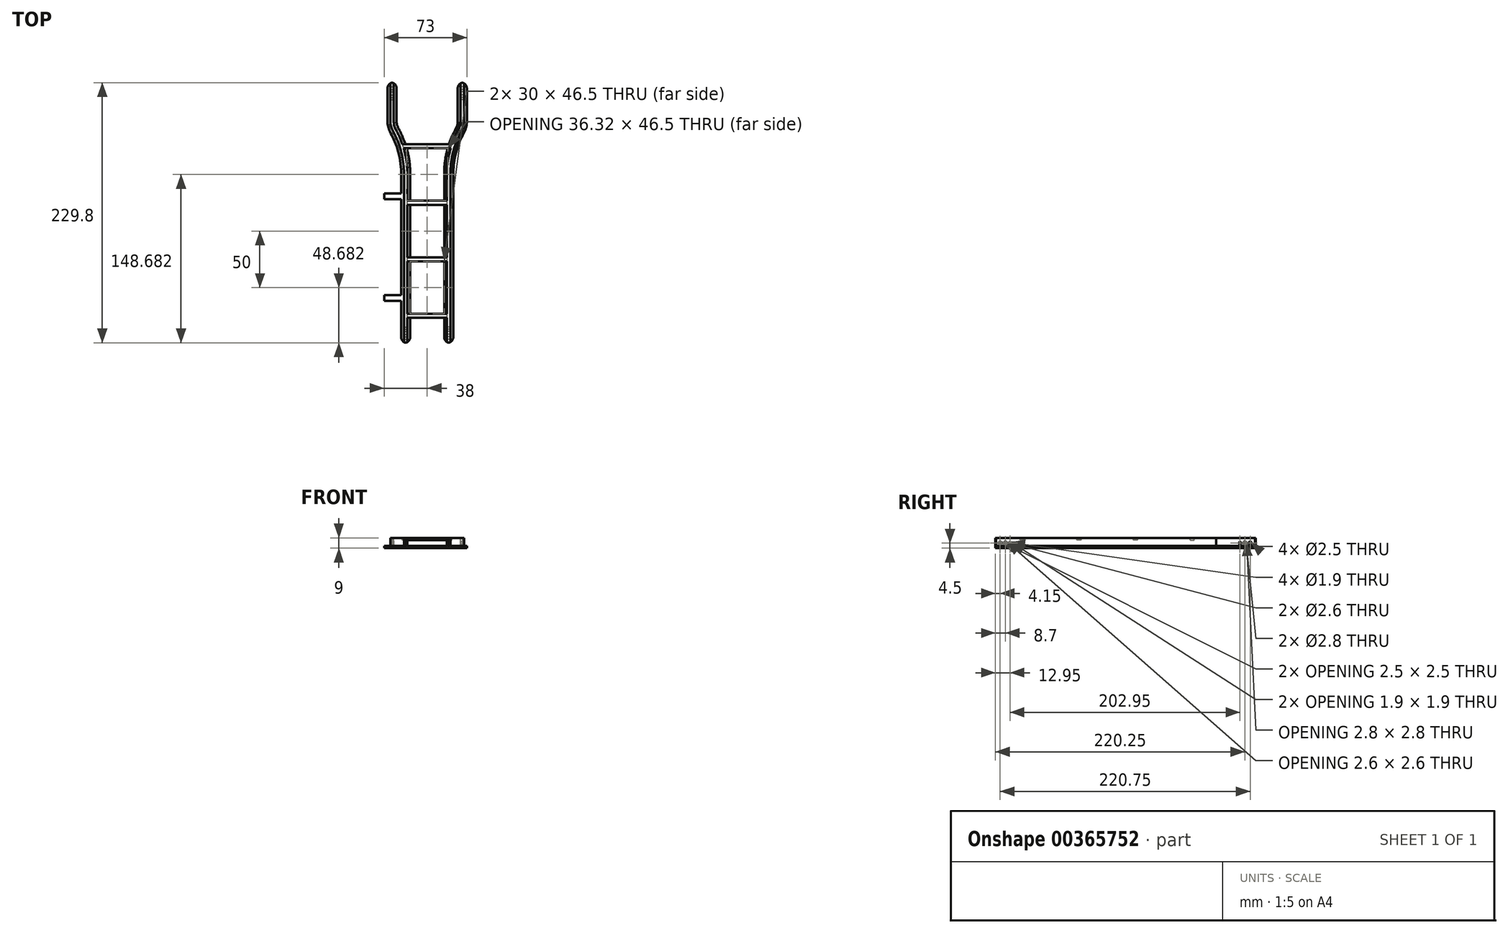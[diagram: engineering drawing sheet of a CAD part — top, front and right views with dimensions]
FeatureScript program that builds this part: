
annotation { "Feature Type Name" : "Feature", "Feature Type Description" : "" }
export const myFeature = defineFeature(function(context is Context, id is Id, definition is map)
    precondition{}
    {
        {
            var Q0;
            Q0=qCreatedBy(makeId("Front.planeOp"),FACE);
            var sketch = newSketch(context, id + "F0", { "sketchPlane" : qUnion([Q0])});
            skLineSegment(sketch, "E0.bottom", {"start": v(-15, 0) * mm, "end": v(-23, 0) * mm});
            skLineSegment(sketch, "E0.top", {"start": v(-15, 9) * mm, "end": v(-23, 9) * mm});
            skLineSegment(sketch, "E0.left", {"start": v(-15, 0) * mm, "end": v(-15, 2) * mm});
            skLineSegment(sketch, "E0.right", {"start": v(-23, 0) * mm, "end": v(-23, 2) * mm});
            skLineSegment(sketch, "E1.bottom", {"start": v(-23, 7) * mm, "end": v(-21, 7) * mm});
            skLineSegment(sketch, "E1.top", {"start": v(-23, 2) * mm, "end": v(-21, 2) * mm});
            skLineSegment(sketch, "E1.right", {"start": v(-20.5, 6.5) * mm, "end": v(-20.5, 2.5) * mm});
            skLineSegment(sketch, "E2.bottom", {"start": v(-17, 7) * mm, "end": v(-15, 7) * mm});
            skLineSegment(sketch, "E2.top", {"start": v(-17, 2) * mm, "end": v(-15, 2) * mm});
            skLineSegment(sketch, "E2.left", {"start": v(-17.5, 6.5) * mm, "end": v(-17.5, 2.5) * mm});
            skLineSegment(sketch, "E3", {"start": v(-19, 9) * mm, "end": v(-19, -4.59) * mm, "construction": true});
            skPoint(sketch, "E3.endSnap0", {"position": v(-19, 0) * mm});
            skLineSegment(sketch, "E4.trimOffspring", {"start": v(-15, 7) * mm, "end": v(-15, 9) * mm});
            skLineSegment(sketch, "E5.trimOffspring", {"start": v(-23, 7) * mm, "end": v(-23, 9) * mm});
            skPoint(sketch, "E6.visualSharp", {"position": v(-20.5, 7) * mm});
            skArc(sketch, "E6.filletArc", {"start": v(-20.5, 6.5) * mm, "mid": v(-20.65, 6.85) * mm, "end": v(-21, 7) * mm});
            skPoint(sketch, "E7.visualSharp", {"position": v(-17.5, 7) * mm});
            skArc(sketch, "E7.filletArc", {"start": v(-17, 7) * mm, "mid": v(-17.35, 6.85) * mm, "end": v(-17.5, 6.5) * mm});
            skPoint(sketch, "E8.visualSharp", {"position": v(-17.5, 2) * mm});
            skArc(sketch, "E8.filletArc", {"start": v(-17.5, 2.5) * mm, "mid": v(-17.35, 2.15) * mm, "end": v(-17, 2) * mm});
            skPoint(sketch, "E9.visualSharp", {"position": v(-20.5, 2) * mm});
            skArc(sketch, "E9.filletArc", {"start": v(-21, 2) * mm, "mid": v(-20.65, 2.15) * mm, "end": v(-20.5, 2.5) * mm});
            skSolve(sketch);
        }
        {
            var Q0;
            Q0=qCreatedBy(makeId("Top.planeOp"),FACE);
            var sketch = newSketch(context, id + "F1", { "sketchPlane" : qUnion([Q0])});
            skLineSegment(sketch, "E10", {"start": v(-35.26, 0) * mm, "end": v(-35.26, 150) * mm});
            skLineSegment(sketch, "E11", {"start": v(-47.26, 230) * mm, "end": v(-47.26, 195) * mm});
            skFitSpline(sketch, "E12", {"points": [v(-35.26, 150) * mm, v(-40.7, 174.86) * mm, v(-47.26, 195) * mm], "startDerivative": vector(-0.38, 53.31) * mm, "endDerivative": vector(-0.87, 58.08) * mm});
            skSolve(sketch);
        }
        {
            var Q0;
            Q0=qSketchRegion(id+"F0",true);
            var Q1;
            Q1=qConstructionFilter(qBodyType(qCreatedBy(id+"F1",EDGE),BodyType.WIRE),ConstructionObject.NO);
            sweep(context, id + "F2", {"profiles" : qUnion([Q0]), "path" : qUnion([Q1])});
        }
        {
            var Q0;
            Q0=qCreatedBy(makeId("Front.planeOp"),FACE);
            var sketch = newSketch(context, id + "F3", { "sketchPlane" : qUnion([Q0])});
            skLineSegment(sketch, "E13.bottom", {"start": v(-17.5, 6.31) * mm, "end": v(-14.7, 6.31) * mm});
            skLineSegment(sketch, "E13.top", {"start": v(-17.5, 10.3) * mm, "end": v(-14.7, 10.3) * mm});
            skLineSegment(sketch, "E13.left", {"start": v(-17.5, 6.31) * mm, "end": v(-17.5, 10.3) * mm});
            skLineSegment(sketch, "E13.right", {"start": v(-14.7, 6.31) * mm, "end": v(-14.7, 10.3) * mm});
            skLineSegment(sketch, "E14.bottom", {"start": v(-20.5, 6.31) * mm, "end": v(-23, 6.31) * mm});
            skLineSegment(sketch, "E14.top", {"start": v(-20.5, 10.3) * mm, "end": v(-23, 10.3) * mm});
            skLineSegment(sketch, "E14.left", {"start": v(-20.5, 6.31) * mm, "end": v(-20.5, 10.3) * mm});
            skLineSegment(sketch, "E14.right", {"start": v(-23, 6.31) * mm, "end": v(-23, 10.3) * mm});
            skSolve(sketch);
        }
        {
            var Q0;
            Q0=makeQuery(id+"F2.opSweep","SWEPT_FACE",FACE,{"disambiguationData":[OSD([sQuery(id+"F0.wireOp",EDGE,"E4.trimOffspring"),sQuery(id+"F1.wireOp",EDGE,"E10")])]});
            var sketch = newSketch(context, id + "F4", { "sketchPlane" : qUnion([Q0])});
            skLineSegment(sketch, "E15.bottom", {"start": v(22.03, 9) * mm, "end": v(25.53, 9) * mm});
            skLineSegment(sketch, "E15.top", {"start": v(22.03, 7) * mm, "end": v(25.53, 7) * mm});
            skLineSegment(sketch, "E15.left", {"start": v(22.03, 9) * mm, "end": v(22.03, 7) * mm});
            skLineSegment(sketch, "E15.right", {"start": v(25.53, 9) * mm, "end": v(25.53, 7) * mm});
            skLineSegment(sketch, "E16.0.1.0", {"start": v(22.03, 2) * mm, "end": v(22.03, 0) * mm});
            skLineSegment(sketch, "E16.0.1.1", {"start": v(22.03, 0) * mm, "end": v(25.53, 0) * mm});
            skLineSegment(sketch, "E16.0.1.2", {"start": v(22.03, 2) * mm, "end": v(25.53, 2) * mm});
            skLineSegment(sketch, "E16.0.1.3", {"start": v(25.53, 2) * mm, "end": v(25.53, 0) * mm});
            skLineSegment(sketch, "E16.1.0.0", {"start": v(72.03, 9) * mm, "end": v(72.03, 7) * mm});
            skLineSegment(sketch, "E16.1.0.1", {"start": v(72.03, 7) * mm, "end": v(75.53, 7) * mm});
            skLineSegment(sketch, "E16.1.0.2", {"start": v(72.03, 9) * mm, "end": v(75.53, 9) * mm});
            skLineSegment(sketch, "E16.1.0.3", {"start": v(75.53, 9) * mm, "end": v(75.53, 7) * mm});
            skLineSegment(sketch, "E16.1.1.0", {"start": v(72.03, 2) * mm, "end": v(72.03, 0) * mm});
            skLineSegment(sketch, "E16.1.1.1", {"start": v(72.03, 0) * mm, "end": v(75.53, 0) * mm});
            skLineSegment(sketch, "E16.1.1.2", {"start": v(72.03, 2) * mm, "end": v(75.53, 2) * mm});
            skLineSegment(sketch, "E16.1.1.3", {"start": v(75.53, 2) * mm, "end": v(75.53, 0) * mm});
            skLineSegment(sketch, "E16.2.0.0", {"start": v(122.03, 9) * mm, "end": v(122.03, 7) * mm});
            skLineSegment(sketch, "E16.2.0.1", {"start": v(122.03, 7) * mm, "end": v(125.53, 7) * mm});
            skLineSegment(sketch, "E16.2.0.2", {"start": v(122.03, 9) * mm, "end": v(125.53, 9) * mm});
            skLineSegment(sketch, "E16.2.0.3", {"start": v(125.53, 9) * mm, "end": v(125.53, 7) * mm});
            skLineSegment(sketch, "E16.2.1.0", {"start": v(122.03, 2) * mm, "end": v(122.03, 0) * mm});
            skLineSegment(sketch, "E16.2.1.1", {"start": v(122.03, 0) * mm, "end": v(125.53, 0) * mm});
            skLineSegment(sketch, "E16.2.1.2", {"start": v(122.03, 2) * mm, "end": v(125.53, 2) * mm});
            skLineSegment(sketch, "E16.2.1.3", {"start": v(125.53, 2) * mm, "end": v(125.53, 0) * mm});
            skLineSegment(sketch, "E16.3.0.0", {"start": v(172.03, 9) * mm, "end": v(172.03, 7) * mm});
            skLineSegment(sketch, "E16.3.0.1", {"start": v(172.03, 7) * mm, "end": v(175.53, 7) * mm});
            skLineSegment(sketch, "E16.3.0.2", {"start": v(172.03, 9) * mm, "end": v(175.53, 9) * mm});
            skLineSegment(sketch, "E16.3.0.3", {"start": v(175.53, 9) * mm, "end": v(175.53, 7) * mm});
            skLineSegment(sketch, "E16.3.1.0", {"start": v(172.03, 2) * mm, "end": v(172.03, 0) * mm});
            skLineSegment(sketch, "E16.3.1.1", {"start": v(172.03, 0) * mm, "end": v(175.53, 0) * mm});
            skLineSegment(sketch, "E16.3.1.2", {"start": v(172.03, 2) * mm, "end": v(175.53, 2) * mm});
            skLineSegment(sketch, "E16.3.1.3", {"start": v(175.53, 2) * mm, "end": v(175.53, 0) * mm});
            skLineSegment(sketch, "E16.direction1", {"start": v(22.03, 7) * mm, "end": v(72.03, 7) * mm, "construction": true});
            skLineSegment(sketch, "E16.direction2", {"start": v(22.03, 7) * mm, "end": v(22.03, 0) * mm, "construction": true});
            skSolve(sketch);
        }
        {
            var Q0;
            Q0=qSketchRegion(id+"F4",true);
            extrude(context, id + "F5", {"entities" : qUnion([Q0]), "operationType" : NewBodyOperationType.ADD, "depth" : 15 * mm});
        }
        {
            var Q0;
            Q0=makeQuery(id+"F5.opExtrude","CAP_FACE",FACE,{"disambiguationData":[OSD([sQuery(id+"F4.wireOp",EDGE,"E16.3.0.0"),sQuery(id+"F4.wireOp",EDGE,"E16.3.0.1"),sQuery(id+"F4.wireOp",EDGE,"E16.3.0.2"),sQuery(id+"F4.wireOp",EDGE,"E16.3.0.3")])],"isStart":true});
            var sketch = newSketch(context, id + "F6", { "sketchPlane" : qUnion([Q0])});
            skLineSegment(sketch, "E17.0", {"start": v(-172.03, 7) * mm, "end": v(-175.53, 7) * mm});
            skLineSegment(sketch, "E18.0.0", {"start": v(-175.53, 9) * mm, "end": v(-175.53, 7) * mm});
            skLineSegment(sketch, "E18.0.1", {"start": v(-175.53, 7) * mm, "end": v(-172.03, 7) * mm});
            skLineSegment(sketch, "E18.0.2", {"start": v(-172.03, 7) * mm, "end": v(-172.03, 9) * mm});
            skLineSegment(sketch, "E18.0.3", {"start": v(-172.03, 9) * mm, "end": v(-175.53, 9) * mm});
            skLineSegment(sketch, "E19.0.0", {"start": v(-175.53, 2) * mm, "end": v(-175.53, 0) * mm});
            skLineSegment(sketch, "E19.0.1", {"start": v(-175.53, 0) * mm, "end": v(-172.03, 0) * mm});
            skLineSegment(sketch, "E19.0.2", {"start": v(-172.03, 0) * mm, "end": v(-172.03, 2) * mm});
            skLineSegment(sketch, "E19.0.3", {"start": v(-172.03, 2) * mm, "end": v(-175.53, 2) * mm});
            skSolve(sketch);
        }
        {
            var Q0;
            Q0=qSketchRegion(id+"F6",true);
            extrude(context, id + "F7", {"entities" : qUnion([Q0]), "operationType" : NewBodyOperationType.ADD, "endBound" : BoundingType.UP_TO_NEXT, "depth" : 25 * mm});
        }
        {
            var Q0;
            Q0 = qSketchRegion(id + "F3", true);
            var Q1;
            Q1 = qConstructionFilter(qBodyType(qCreatedBy(id + "F1" ,EDGE), BodyType.WIRE), ConstructionObject.NO);
            sweep(context, id + "F8", {"operationType" : NewBodyOperationType.REMOVE, "profiles" : qUnion([Q0]), "path" : qUnion([Q1])});
        }
        {
            var Q0;
            Q0=qCreatedBy(makeId("Right.planeOp"),FACE);
            var sketch = newSketch(context, id + "F9", { "sketchPlane" : qUnion([Q0])});
            skLineSegment(sketch, "E20.0.0", {"start": v(25.53, 7) * mm, "end": v(25.53, 9) * mm});
            skLineSegment(sketch, "E20.0.1", {"start": v(25.53, 9) * mm, "end": v(22.03, 9) * mm});
            skLineSegment(sketch, "E20.0.2", {"start": v(22.03, 9) * mm, "end": v(22.03, 7) * mm});
            skLineSegment(sketch, "E20.0.3", {"start": v(22.03, 7) * mm, "end": v(25.53, 7) * mm});
            skLineSegment(sketch, "E21.0.0", {"start": v(75.53, 7) * mm, "end": v(75.53, 9) * mm});
            skLineSegment(sketch, "E21.0.1", {"start": v(75.53, 9) * mm, "end": v(72.03, 9) * mm});
            skLineSegment(sketch, "E21.0.2", {"start": v(72.03, 9) * mm, "end": v(72.03, 7) * mm});
            skLineSegment(sketch, "E21.0.3", {"start": v(72.03, 7) * mm, "end": v(75.53, 7) * mm});
            skLineSegment(sketch, "E22.0.0", {"start": v(175.53, 7) * mm, "end": v(175.53, 9) * mm});
            skLineSegment(sketch, "E22.0.1", {"start": v(175.53, 9) * mm, "end": v(172.03, 9) * mm});
            skLineSegment(sketch, "E22.0.2", {"start": v(172.03, 9) * mm, "end": v(172.03, 7) * mm});
            skLineSegment(sketch, "E22.0.3", {"start": v(172.03, 7) * mm, "end": v(175.53, 7) * mm});
            skLineSegment(sketch, "E23.0.0", {"start": v(125.53, 7) * mm, "end": v(125.53, 9) * mm});
            skLineSegment(sketch, "E23.0.1", {"start": v(125.53, 9) * mm, "end": v(122.03, 9) * mm});
            skLineSegment(sketch, "E23.0.2", {"start": v(122.03, 9) * mm, "end": v(122.03, 7) * mm});
            skLineSegment(sketch, "E23.0.3", {"start": v(122.03, 7) * mm, "end": v(125.53, 7) * mm});
            skSolve(sketch);
        }
        {
            var Q0;
            Q0 = qSketchRegion(id + "F9", true);
            var Q1;
            Q1=makeQuery(id+"F8.boolean.opBoolean","SPLIT",BODY,{"disambiguationData":[OD(0.0)],"derivedFrom":makeQuery(id+"F2.opSweep","SWEPT_BODY",BODY,{"disambiguationData":[OSD([sQuery(id+"F0.wireOp",EDGE,"E0.bottom"),sQuery(id+"F0.wireOp",EDGE,"E0.top"),sQuery(id+"F0.wireOp",EDGE,"E0.left"),sQuery(id+"F0.wireOp",EDGE,"E0.right"),sQuery(id+"F0.wireOp",EDGE,"E1.bottom"),sQuery(id+"F0.wireOp",EDGE,"E1.top"),sQuery(id+"F0.wireOp",EDGE,"E1.right"),sQuery(id+"F0.wireOp",EDGE,"E2.bottom"),sQuery(id+"F0.wireOp",EDGE,"E2.top"),sQuery(id+"F0.wireOp",EDGE,"E2.left"),sQuery(id+"F0.wireOp",EDGE,"E4.trimOffspring"),sQuery(id+"F0.wireOp",EDGE,"E5.trimOffspring"),sQuery(id+"F0.wireOp",EDGE,"E6.filletArc"),sQuery(id+"F0.wireOp",EDGE,"E7.filletArc"),sQuery(id+"F0.wireOp",EDGE,"E8.filletArc"),sQuery(id+"F0.wireOp",EDGE,"E9.filletArc"),sQuery(id+"F1.wireOp",EDGE,"E11")])]})});
            extrude(context, id + "F10", {"entities" : qUnion([Q0]), "operationType" : NewBodyOperationType.ADD, "endBound" : BoundingType.UP_TO_BODY, "oppositeDirection" : true, "depth" : 25 * mm, "endBoundEntityBody" : qUnion([Q1]), "offsetDistance" : 25 * mm});
        }
        {
            var Q0;
            {var subQ0=sQuery(id+"F1.wireOp",EDGE,"E10");Q0=makeQuery(id+"F8.boolean.opBoolean","MERGE",FACE,{"derivedFrom":[makeQuery(id+"F2.opSweep","SWEPT_FACE",FACE,{"disambiguationData":[OSD([sQuery(id+"F0.wireOp",EDGE,"E2.left"),subQ0])]}),makeQuery(id+"F8.opSweep","SWEPT_FACE",FACE,{"disambiguationData":[OSD([subQ0,sQuery(id+"F3.wireOp",EDGE,"E13.left")])]})]});}
            var sketch = newSketch(context, id + "F11", { "sketchPlane" : qUnion([Q0])});
            skCircle(sketch, "E24", {"center": v(4.25, 4.5) * mm, "radius": 1.25 * mm});
            skCircle(sketch, "E25", {"center": v(8.8, 4.5) * mm, "radius": 1.3 * mm});
            skCircle(sketch, "E26", {"center": v(225, 4.5) * mm, "radius": 1.25 * mm});
            skCircle(sketch, "E27", {"center": v(220.35, 4.5) * mm, "radius": 1.4 * mm});
            skCircle(sketch, "E28", {"center": v(13.05, 4.5) * mm, "radius": 0.95 * mm});
            skCircle(sketch, "E29", {"center": v(216, 4.5) * mm, "radius": 0.95 * mm});
            skSolve(sketch);
        }
        {
            var Q0;
            Q0 = qSketchRegion(id + "F11", true);
            extrude(context, id + "F12", {"entities" : qUnion([Q0]), "operationType" : NewBodyOperationType.REMOVE, "endBound" : BoundingType.THROUGH_ALL, "oppositeDirection" : true, "depth" : 25 * mm, "offsetDistance" : 25 * mm});
        }
        {
            var Q0;
            Q0=makeQuery(id+"F2.opSweep","CAP_EDGE",EDGE,{"disambiguationData":[OSD([sQuery(id+"F0.wireOp",EDGE,"E0.left"),sQuery(id+"F1.wireOp",VERTEX,"E10.start")])],"isStart":true});
            var Q1;
            Q1=makeQuery(id+"F2.opSweep","CAP_EDGE",EDGE,{"disambiguationData":[OSD([sQuery(id+"F0.wireOp",EDGE,"E0.right"),sQuery(id+"F1.wireOp",VERTEX,"E10.start")])],"isStart":true});
            var Q2;
            Q2=makeQuery(id+"F2.opSweep","CAP_EDGE",EDGE,{"disambiguationData":[OSD([sQuery(id+"F0.wireOp",EDGE,"E0.right"),sQuery(id+"F1.wireOp",VERTEX,"E11.start")])],"isStart":false});
            var Q3;
            Q3=makeQuery(id+"F2.opSweep","CAP_EDGE",EDGE,{"disambiguationData":[OSD([sQuery(id+"F0.wireOp",EDGE,"E0.left"),sQuery(id+"F1.wireOp",VERTEX,"E11.start")])],"isStart":false});
            fillet(context, id + "F13", {"entities" : qUnion([Q0, Q1, Q2, Q3]), "radius" : 5 * mm, "tangentPropagation" : true, "allowEdgeOverflow" : false});
        }
        {
            var Q0;
            Q0=makeQuery(id+"F8.boolean.opBoolean","SPLIT",BODY,{"disambiguationData":[OD(0.0)],"derivedFrom":makeQuery(id+"F2.opSweep","SWEPT_BODY",BODY,{"disambiguationData":[OSD([sQuery(id+"F0.wireOp",EDGE,"E0.bottom"),sQuery(id+"F0.wireOp",EDGE,"E0.top"),sQuery(id+"F0.wireOp",EDGE,"E0.left"),sQuery(id+"F0.wireOp",EDGE,"E0.right"),sQuery(id+"F0.wireOp",EDGE,"E1.bottom"),sQuery(id+"F0.wireOp",EDGE,"E1.top"),sQuery(id+"F0.wireOp",EDGE,"E1.right"),sQuery(id+"F0.wireOp",EDGE,"E2.bottom"),sQuery(id+"F0.wireOp",EDGE,"E2.top"),sQuery(id+"F0.wireOp",EDGE,"E2.left"),sQuery(id+"F0.wireOp",EDGE,"E4.trimOffspring"),sQuery(id+"F0.wireOp",EDGE,"E5.trimOffspring"),sQuery(id+"F0.wireOp",EDGE,"E6.filletArc"),sQuery(id+"F0.wireOp",EDGE,"E7.filletArc"),sQuery(id+"F0.wireOp",EDGE,"E8.filletArc"),sQuery(id+"F0.wireOp",EDGE,"E9.filletArc"),sQuery(id+"F1.wireOp",EDGE,"E11")])]})});
            var Q1;
            Q1=makeQuery(id+"F5.opExtrude","CAP_FACE",FACE,{"disambiguationData":[OSD([sQuery(id+"F4.wireOp",EDGE,"E15.bottom"),sQuery(id+"F4.wireOp",EDGE,"E15.top"),sQuery(id+"F4.wireOp",EDGE,"E15.left"),sQuery(id+"F4.wireOp",EDGE,"E15.right")])],"isStart":false});
            mirror(context, id + "F14", {"operationType" : NewBodyOperationType.ADD, "entities" : qUnion([Q0]), "mirrorPlane" : qUnion([Q1])});
        }
        {
            var Q0;
            Q0=makeQuery(id+"F2.opSweep","SWEPT_FACE",FACE,{"disambiguationData":[OSD([sQuery(id+"F0.wireOp",EDGE,"E0.right"),sQuery(id+"F1.wireOp",EDGE,"E10")])]});
            var sketch = newSketch(context, id + "F15", { "sketchPlane" : qUnion([Q0])});
            skLineSegment(sketch, "E30.bottom", {"start": v(-37.1, 2) * mm, "end": v(-42.1, 2) * mm});
            skLineSegment(sketch, "E30.top", {"start": v(-37.1, 0) * mm, "end": v(-42.1, 0) * mm});
            skLineSegment(sketch, "E30.left", {"start": v(-37.1, 2) * mm, "end": v(-37.1, 0) * mm});
            skLineSegment(sketch, "E30.right", {"start": v(-42.1, 2) * mm, "end": v(-42.1, 0) * mm});
            skLineSegment(sketch, "E31.bottom", {"start": v(-132.1, 2) * mm, "end": v(-127.1, 2) * mm});
            skLineSegment(sketch, "E31.top", {"start": v(-132.1, 0) * mm, "end": v(-127.1, 0) * mm});
            skLineSegment(sketch, "E31.left", {"start": v(-132.1, 2) * mm, "end": v(-132.1, 0) * mm});
            skLineSegment(sketch, "E31.right", {"start": v(-127.1, 2) * mm, "end": v(-127.1, 0) * mm});
            skSolve(sketch);
        }
        {
            var Q0;
            Q0 = qSketchRegion(id + "F15", true);
            extrude(context, id + "F16", {"entities" : qUnion([Q0]), "operationType" : NewBodyOperationType.ADD, "depth" : 15 * mm, "offsetDistance" : 25 * mm});
        }
    });
